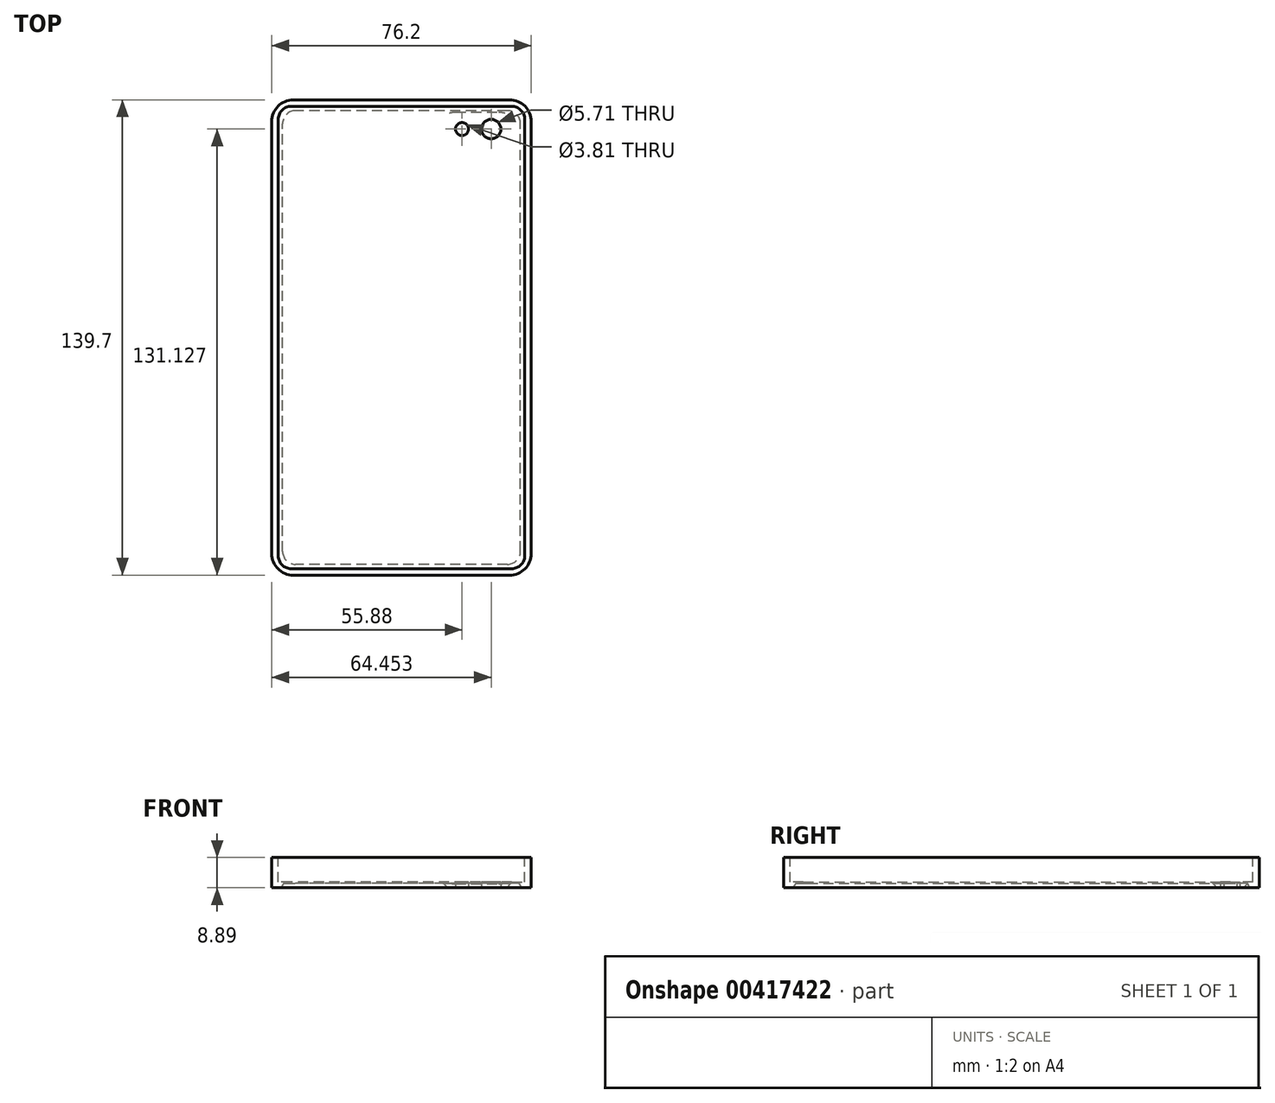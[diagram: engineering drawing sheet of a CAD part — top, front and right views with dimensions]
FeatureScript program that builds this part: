
annotation { "Feature Type Name" : "Feature", "Feature Type Description" : "" }
export const myFeature = defineFeature(function(context is Context, id is Id, definition is map)
    precondition{}
    {
        {
            var Q0;
            Q0=qCreatedBy(makeId("Top.planeOp"),FACE);
            var sketch = newSketch(context, id + "F0", { "sketchPlane" : qUnion([Q0])});
            skLineSegment(sketch, "E0.bottom", {"start": v(31.75, -69.85) * mm, "end": v(-31.75, -69.85) * mm});
            skLineSegment(sketch, "E0.top", {"start": v(31.75, 69.85) * mm, "end": v(-31.75, 69.85) * mm});
            skLineSegment(sketch, "E0.left", {"start": v(38.1, -63.5) * mm, "end": v(38.1, 63.5) * mm});
            skLineSegment(sketch, "E0.right", {"start": v(-38.1, -63.5) * mm, "end": v(-38.1, 63.5) * mm});
            skPoint(sketch, "E0.middle", {"position": v(0, 0) * mm});
            skPoint(sketch, "E1.visualSharp", {"position": v(-38.1, 69.85) * mm});
            skArc(sketch, "E1.filletArc", {"start": v(-31.75, 69.85) * mm, "mid": v(-36.24, 68) * mm, "end": v(-38.1, 63.5) * mm});
            skPoint(sketch, "E2.visualSharp", {"position": v(38.1, 69.85) * mm});
            skArc(sketch, "E2.filletArc", {"start": v(38.1, 63.5) * mm, "mid": v(36.24, 68) * mm, "end": v(31.75, 69.85) * mm});
            skPoint(sketch, "E3.visualSharp", {"position": v(38.1, -69.85) * mm});
            skArc(sketch, "E3.filletArc", {"start": v(31.75, -69.85) * mm, "mid": v(36.24, -68) * mm, "end": v(38.1, -63.5) * mm});
            skPoint(sketch, "E4.visualSharp", {"position": v(-38.1, -69.85) * mm});
            skArc(sketch, "E4.filletArc", {"start": v(-38.1, -63.5) * mm, "mid": v(-36.24, -68) * mm, "end": v(-31.75, -69.85) * mm});
            skSolve(sketch);
        }
        {
            var Q0;
            Q0=makeQuery(id+"F0.imprint","IMPRINT",FACE,{"disambiguationData":[TD([[makeQuery(id+"F0.imprint","IMPRINT",EDGE,{"derivedFrom":sQuery(id+"F0.wireOp",EDGE,"E0.bottom")}),-1.0]])]});
            extrude(context, id + "F1", {"entities" : qUnion([Q0]), "depth" : 7.62 * mm});
        }
        {
            var Q0;
            Q0=makeQuery(id+"F1.opExtrude","CAP_FACE",FACE,{"disambiguationData":[OSD([sQuery(id+"F0.wireOp",EDGE,"E0.bottom"),sQuery(id+"F0.wireOp",EDGE,"E0.top"),sQuery(id+"F0.wireOp",EDGE,"E0.left"),sQuery(id+"F0.wireOp",EDGE,"E0.right"),sQuery(id+"F0.wireOp",EDGE,"E1.filletArc"),sQuery(id+"F0.wireOp",EDGE,"E2.filletArc"),sQuery(id+"F0.wireOp",EDGE,"E3.filletArc"),sQuery(id+"F0.wireOp",EDGE,"E4.filletArc")])],"isStart":false});
            var sketch = newSketch(context, id + "F2", { "sketchPlane" : qUnion([Q0])});
            skLineSegment(sketch, "E5.bottom", {"start": v(32.38, -67.95) * mm, "end": v(-32.39, -67.95) * mm});
            skLineSegment(sketch, "E5.top", {"start": v(32.39, 67.95) * mm, "end": v(-32.38, 67.95) * mm});
            skLineSegment(sketch, "E5.left", {"start": v(36.2, -64.14) * mm, "end": v(36.2, 64.14) * mm});
            skLineSegment(sketch, "E5.right", {"start": v(-36.2, -64.14) * mm, "end": v(-36.2, 64.13) * mm});
            skPoint(sketch, "E5.middle", {"position": v(0, 0) * mm});
            skPoint(sketch, "E6.visualSharp", {"position": v(-36.2, 67.94) * mm});
            skArc(sketch, "E6.filletArc", {"start": v(-32.38, 67.94) * mm, "mid": v(-35.08, 66.83) * mm, "end": v(-36.2, 64.13) * mm});
            skPoint(sketch, "E7.visualSharp", {"position": v(36.2, 67.95) * mm});
            skArc(sketch, "E7.filletArc", {"start": v(36.2, 64.14) * mm, "mid": v(35.08, 66.83) * mm, "end": v(32.39, 67.95) * mm});
            skPoint(sketch, "E8.visualSharp", {"position": v(-36.2, -67.95) * mm});
            skArc(sketch, "E8.filletArc", {"start": v(-36.2, -64.14) * mm, "mid": v(-35.08, -66.83) * mm, "end": v(-32.39, -67.95) * mm});
            skPoint(sketch, "E9.visualSharp", {"position": v(36.2, -67.95) * mm});
            skArc(sketch, "E9.filletArc", {"start": v(32.38, -67.95) * mm, "mid": v(35.08, -66.83) * mm, "end": v(36.2, -64.14) * mm});
            skSolve(sketch);
        }
        {
            var Q0;
            Q0=makeQuery(id+"F2.imprint","IMPRINT",FACE,{"disambiguationData":[TD([[makeQuery(id+"F2.imprint","IMPRINT",EDGE,{"derivedFrom":sQuery(id+"F2.wireOp",EDGE,"E5.bottom")}),-1.0]])]});
            extrude(context, id + "F3", {"entities" : qUnion([Q0]), "operationType" : NewBodyOperationType.REMOVE, "oppositeDirection" : true, "depth" : 7.24 * mm});
        }
        {
            var Q0;
            Q0=makeQuery(id+"F1.opExtrude","CAP_FACE",FACE,{"disambiguationData":[OSD([sQuery(id+"F0.wireOp",EDGE,"E0.bottom"),sQuery(id+"F0.wireOp",EDGE,"E0.top"),sQuery(id+"F0.wireOp",EDGE,"E0.left"),sQuery(id+"F0.wireOp",EDGE,"E0.right"),sQuery(id+"F0.wireOp",EDGE,"E1.filletArc"),sQuery(id+"F0.wireOp",EDGE,"E2.filletArc"),sQuery(id+"F0.wireOp",EDGE,"E3.filletArc"),sQuery(id+"F0.wireOp",EDGE,"E4.filletArc")])],"isStart":true});
            var sketch = newSketch(context, id + "F4", { "sketchPlane" : qUnion([Q0])});
            skLineSegment(sketch, "E10.bottom", {"start": v(15.88, -56.52) * mm, "end": v(28.57, -56.52) * mm});
            skLineSegment(sketch, "E10.top", {"start": v(15.88, -66.04) * mm, "end": v(28.58, -66.04) * mm});
            skLineSegment(sketch, "E10.left", {"start": v(12.7, -59.7) * mm, "end": v(12.7, -62.87) * mm});
            skLineSegment(sketch, "E10.right", {"start": v(31.75, -59.7) * mm, "end": v(31.75, -62.87) * mm});
            skPoint(sketch, "E10.middle", {"position": v(22.23, -61.28) * mm});
            skLineSegment(sketch, "E11", {"start": v(0, 69.85) * mm, "end": v(0, -69.85) * mm, "construction": true});
            skLineSegment(sketch, "E12", {"start": v(-38.1, 0) * mm, "end": v(38.1, 0) * mm, "construction": true});
            skPoint(sketch, "E13.visualSharp", {"position": v(12.7, -56.52) * mm});
            skArc(sketch, "E13.filletArc", {"start": v(15.88, -56.52) * mm, "mid": v(13.63, -57.44) * mm, "end": v(12.7, -59.7) * mm});
            skPoint(sketch, "E14.visualSharp", {"position": v(31.75, -56.52) * mm});
            skArc(sketch, "E14.filletArc", {"start": v(31.75, -59.7) * mm, "mid": v(30.82, -57.44) * mm, "end": v(28.57, -56.52) * mm});
            skPoint(sketch, "E15.visualSharp", {"position": v(31.75, -66.04) * mm});
            skArc(sketch, "E15.filletArc", {"start": v(28.58, -66.04) * mm, "mid": v(30.82, -65.11) * mm, "end": v(31.75, -62.87) * mm});
            skPoint(sketch, "E16.visualSharp", {"position": v(12.7, -66.04) * mm});
            skArc(sketch, "E16.filletArc", {"start": v(12.7, -62.87) * mm, "mid": v(13.63, -65.11) * mm, "end": v(15.88, -66.04) * mm});
            skSolve(sketch);
        }
        {
            var Q0;
            Q0 = qSketchRegion(id + "F4", true);
            extrude(context, id + "F5", {"entities" : qUnion([Q0]), "operationType" : NewBodyOperationType.ADD, "depth" : 1.27 * mm, "hasDraft" : true, "draftAngle" : 15 * degree, "draftPullDirection" : true});
        }
        {
            var Q0;
            Q0=makeQuery(id+"F5.opExtrude","CAP_FACE",FACE,{"disambiguationData":[OSD([sQuery(id+"F4.wireOp",EDGE,"E10.bottom"),sQuery(id+"F4.wireOp",EDGE,"E10.top"),sQuery(id+"F4.wireOp",EDGE,"E10.left"),sQuery(id+"F4.wireOp",EDGE,"E10.right"),sQuery(id+"F4.wireOp",EDGE,"E13.filletArc"),sQuery(id+"F4.wireOp",EDGE,"E14.filletArc"),sQuery(id+"F4.wireOp",EDGE,"E15.filletArc"),sQuery(id+"F4.wireOp",EDGE,"E16.filletArc")])],"isStart":false});
            fillet(context, id + "F6", {"entities" : qUnion([Q0]), "radius" : 1.27 * mm, "tangentPropagation" : true, "allowEdgeOverflow" : false});
        }
        {
            var Q0;
            Q0=makeQuery(id+"F5.opExtrude","CAP_FACE",FACE,{"disambiguationData":[OSD([sQuery(id+"F4.wireOp",EDGE,"E10.bottom"),sQuery(id+"F4.wireOp",EDGE,"E10.top"),sQuery(id+"F4.wireOp",EDGE,"E10.left"),sQuery(id+"F4.wireOp",EDGE,"E10.right"),sQuery(id+"F4.wireOp",EDGE,"E13.filletArc"),sQuery(id+"F4.wireOp",EDGE,"E14.filletArc"),sQuery(id+"F4.wireOp",EDGE,"E15.filletArc"),sQuery(id+"F4.wireOp",EDGE,"E16.filletArc")])],"isStart":false});
            var sketch = newSketch(context, id + "F7", { "sketchPlane" : qUnion([Q0])});
            skLineSegment(sketch, "E17", {"start": v(14.01, -61.28) * mm, "end": v(30.44, -61.28) * mm, "construction": true});
            skCircle(sketch, "E18", {"center": v(17.78, -61.28) * mm, "radius": 1.9 * mm});
            skCircle(sketch, "E19", {"center": v(26.35, -61.28) * mm, "radius": 2.86 * mm});
            skLineSegment(sketch, "E20", {"start": v(22.23, -57.83) * mm, "end": v(22.23, -64.73) * mm, "construction": true});
            skSolve(sketch);
        }
        {
            var Q0;
            Q0 = qSketchRegion(id + "F7", true);
            extrude(context, id + "F8", {"entities" : qUnion([Q0]), "operationType" : NewBodyOperationType.REMOVE, "endBound" : BoundingType.THROUGH_ALL, "oppositeDirection" : true, "depth" : 25.4 * mm});
        }
        {
            var Q0;
            Q0=makeQuery(id+"F1.opExtrude","CAP_FACE",FACE,{"disambiguationData":[OSD([sQuery(id+"F0.wireOp",EDGE,"E0.bottom"),sQuery(id+"F0.wireOp",EDGE,"E0.top"),sQuery(id+"F0.wireOp",EDGE,"E0.left"),sQuery(id+"F0.wireOp",EDGE,"E0.right"),sQuery(id+"F0.wireOp",EDGE,"E1.filletArc"),sQuery(id+"F0.wireOp",EDGE,"E2.filletArc"),sQuery(id+"F0.wireOp",EDGE,"E3.filletArc"),sQuery(id+"F0.wireOp",EDGE,"E4.filletArc")])],"isStart":true});
            var sketch = newSketch(context, id + "F9", { "sketchPlane" : qUnion([Q0])});
            skLineSegment(sketch, "E21.bottom", {"start": v(31.11, 66.68) * mm, "end": v(-31.11, 66.68) * mm});
            skLineSegment(sketch, "E21.top", {"start": v(31.11, -66.68) * mm, "end": v(-31.11, -66.68) * mm});
            skLineSegment(sketch, "E21.left", {"start": v(34.92, 62.87) * mm, "end": v(34.92, -62.87) * mm});
            skLineSegment(sketch, "E21.right", {"start": v(-34.92, 62.87) * mm, "end": v(-34.92, -62.87) * mm});
            skPoint(sketch, "E21.middle", {"position": v(0, 0) * mm});
            skLineSegment(sketch, "E22", {"start": v(0, 69.85) * mm, "end": v(0, -69.85) * mm, "construction": true});
            skLineSegment(sketch, "E23", {"start": v(-38.1, 0) * mm, "end": v(38.1, 0) * mm, "construction": true});
            skPoint(sketch, "E24.visualSharp", {"position": v(-34.92, 66.68) * mm});
            skArc(sketch, "E24.filletArc", {"start": v(-31.11, 66.68) * mm, "mid": v(-33.8, 65.56) * mm, "end": v(-34.92, 62.87) * mm});
            skPoint(sketch, "E25.visualSharp", {"position": v(34.92, 66.68) * mm});
            skArc(sketch, "E25.filletArc", {"start": v(34.92, 62.87) * mm, "mid": v(33.8, 65.56) * mm, "end": v(31.11, 66.68) * mm});
            skPoint(sketch, "E26.visualSharp", {"position": v(34.92, -66.68) * mm});
            skArc(sketch, "E26.filletArc", {"start": v(31.11, -66.68) * mm, "mid": v(33.8, -65.56) * mm, "end": v(34.92, -62.87) * mm});
            skPoint(sketch, "E27.visualSharp", {"position": v(-34.92, -66.68) * mm});
            skArc(sketch, "E27.filletArc", {"start": v(-34.92, -62.87) * mm, "mid": v(-33.8, -65.56) * mm, "end": v(-31.11, -66.68) * mm});
            skSolve(sketch);
        }
        {
            var Q0;
            Q0=makeQuery(id+"F9.imprint","IMPRINT",FACE,{"disambiguationData":[TD([[makeQuery(id+"F9.imprint","IMPRINT",EDGE,{"derivedFrom":sQuery(id+"F9.wireOp",EDGE,"E21.bottom")}),-1.0]])]});
            extrude(context, id + "F10", {"entities" : qUnion([Q0]), "operationType" : NewBodyOperationType.ADD, "depth" : 1.27 * mm});
        }
        {
            var Q0;
            Q0=makeQuery(id+"F10.opExtrude","CAP_EDGE",EDGE,{"disambiguationData":[OSD([sQuery(id+"F9.wireOp",EDGE,"E21.bottom")])],"isStart":false});
            var Q1;
            Q1=makeQuery(id+"F1.opExtrude","CAP_FACE",FACE,{"disambiguationData":[OSD([sQuery(id+"F0.wireOp",EDGE,"E0.bottom"),sQuery(id+"F0.wireOp",EDGE,"E0.top"),sQuery(id+"F0.wireOp",EDGE,"E0.left"),sQuery(id+"F0.wireOp",EDGE,"E0.right"),sQuery(id+"F0.wireOp",EDGE,"E1.filletArc"),sQuery(id+"F0.wireOp",EDGE,"E2.filletArc"),sQuery(id+"F0.wireOp",EDGE,"E3.filletArc"),sQuery(id+"F0.wireOp",EDGE,"E4.filletArc")])],"isStart":true});
            fillet(context, id + "F11", {"entities" : qUnion([Q0, Q1]), "radius" : 0.64 * mm, "tangentPropagation" : true, "allowEdgeOverflow" : false});
        }
    });
